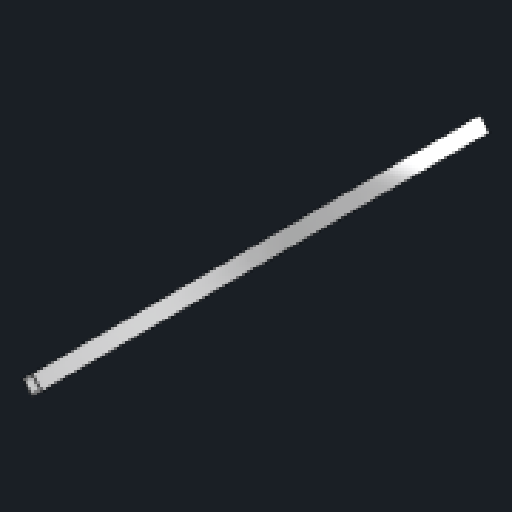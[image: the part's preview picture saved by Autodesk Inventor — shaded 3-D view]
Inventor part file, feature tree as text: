
AUTODESK INVENTOR PART (.ipt)
format: ipt  version: 2023.2 (Build 272271030, 271C)  size: 116,224 bytes
history: native  units: mm
features: extrude x1, sketch x1
ambient origin geometry x8: Origin, YZ Plane, XZ Plane, XY Plane, X Axis, Y Axis, Z Axis, Center Point
bodies: Body1 (feature_tree)
feature tree (2):
  extrude  "Extrusion2"  Depth=0.396875mm
  sketch  "Sketch1"  dims[d4=3.175mm d5=0.396875mm d6=101.0mm d7=0.0mm]
